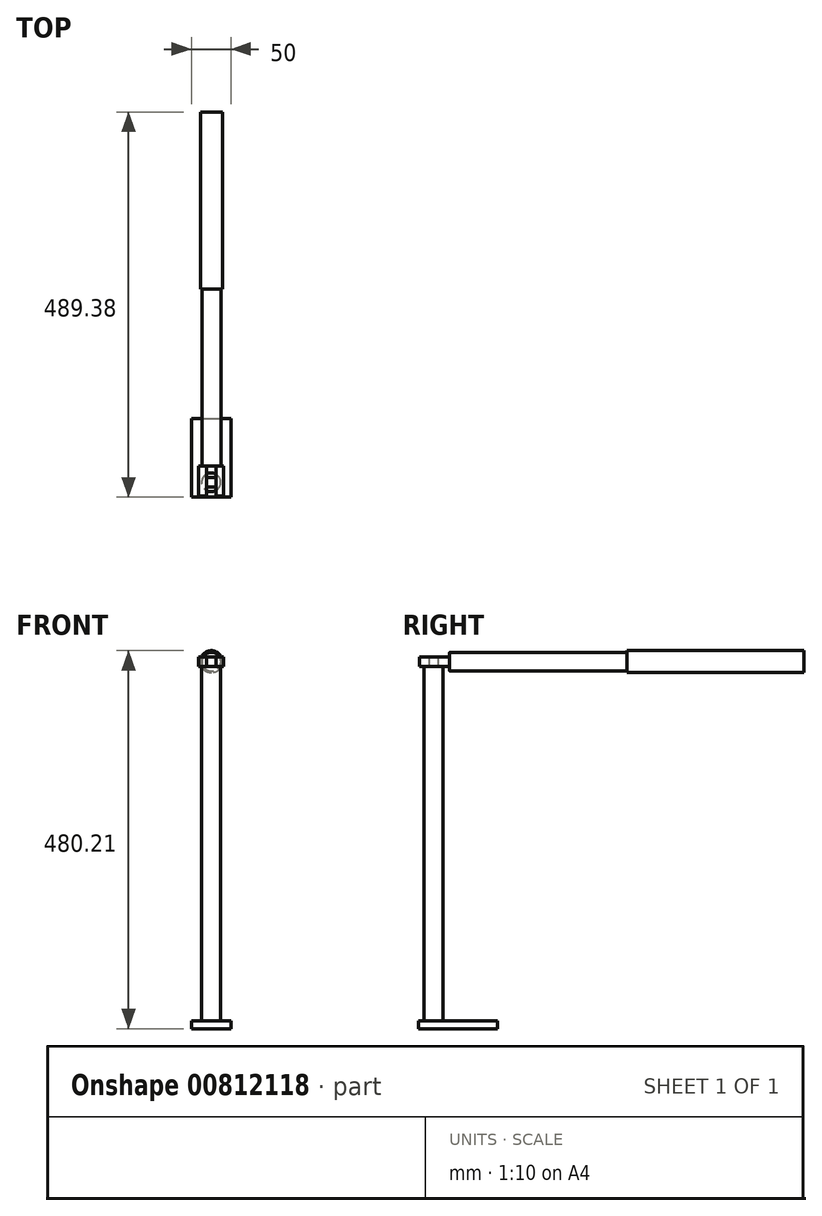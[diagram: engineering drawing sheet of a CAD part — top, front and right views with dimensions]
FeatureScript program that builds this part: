
annotation { "Feature Type Name" : "Feature", "Feature Type Description" : "" }
export const myFeature = defineFeature(function(context is Context, id is Id, definition is map)
    precondition{}
    {
        {
            var Q0;
            Q0=qCreatedBy(makeId("Top.planeOp"),FACE);
            var sketch = newSketch(context, id + "F0", { "sketchPlane" : qUnion([Q0])});
            skLineSegment(sketch, "E0.bottom", {"start": v(-96.82, -89.7) * mm, "end": v(-46.82, -89.7) * mm});
            skLineSegment(sketch, "E0.top", {"start": v(-96.82, 10.3) * mm, "end": v(-46.82, 10.3) * mm});
            skLineSegment(sketch, "E0.left", {"start": v(-96.82, -89.7) * mm, "end": v(-96.82, 10.3) * mm});
            skLineSegment(sketch, "E0.right", {"start": v(-46.82, -89.7) * mm, "end": v(-46.82, 10.3) * mm});
            skLineSegment(sketch, "E1.bottom", {"start": v(-96.82, 10.3) * mm, "end": v(-86.82, 10.3) * mm});
            skLineSegment(sketch, "E1.top", {"start": v(-96.82, 30.3) * mm, "end": v(-86.82, 30.3) * mm});
            skLineSegment(sketch, "E1.left", {"start": v(-96.82, 10.3) * mm, "end": v(-96.82, 30.3) * mm});
            skLineSegment(sketch, "E1.right", {"start": v(-86.82, 10.3) * mm, "end": v(-86.82, 30.3) * mm});
            skLineSegment(sketch, "E2.bottom", {"start": v(-46.82, 10.3) * mm, "end": v(-56.82, 10.3) * mm});
            skLineSegment(sketch, "E2.top", {"start": v(-46.82, 30.3) * mm, "end": v(-56.82, 30.3) * mm});
            skLineSegment(sketch, "E2.left", {"start": v(-46.82, 10.3) * mm, "end": v(-46.82, 30.3) * mm});
            skLineSegment(sketch, "E2.right", {"start": v(-56.82, 10.3) * mm, "end": v(-56.82, 30.3) * mm});
            skLineSegment(sketch, "E3.bottom", {"start": v(-86.82, 10.3) * mm, "end": v(-56.82, 10.3) * mm});
            skLineSegment(sketch, "E3.top", {"start": v(-86.82, 50.3) * mm, "end": v(-56.82, 50.3) * mm});
            skLineSegment(sketch, "E3.left", {"start": v(-86.82, 10.3) * mm, "end": v(-86.82, 50.3) * mm});
            skLineSegment(sketch, "E3.right", {"start": v(-56.82, 10.3) * mm, "end": v(-56.82, 50.3) * mm});
            skSolve(sketch);
        }
        {
            var Q0;
            Q0=makeQuery(id+"F0.imprint","IMPRINT",FACE,{"disambiguationData":[TD([[makeQuery(id+"F0.imprint","IMPRINT",EDGE,{"derivedFrom":sQuery(id+"F0.wireOp",EDGE,"E0.bottom")}),1.0]])]});
            var Q1;
            {var subQ0=sQuery(id+"F0.wireOp",EDGE,"E1.bottom");Q1=makeQuery(id+"F0.imprint","IMPRINT",FACE,{"disambiguationData":[TD([[makeQuery(id+"F0.imprint","IMPRINT",EDGE,{"derivedFrom":subQ0}),1.0]])]});}
            var Q2;
            {var subQ3=sQuery(id+"F0.wireOp",EDGE,"E3.bottom");Q2=makeQuery(id+"F0.imprint","IMPRINT",FACE,{"disambiguationData":[TD([[makeQuery(id+"F0.imprint","IMPRINT",EDGE,{"derivedFrom":subQ3}),1.0]])]});}
            var Q3;
            {var subQ0=sQuery(id+"F0.wireOp",EDGE,"E2.bottom");Q3=makeQuery(id+"F0.imprint","IMPRINT",FACE,{"disambiguationData":[TD([[makeQuery(id+"F0.imprint","IMPRINT",EDGE,{"derivedFrom":subQ0}),-1.0]])]});}
            extrude(context, id + "F1", {"entities" : qUnion([Q0, Q1, Q2, Q3]), "depth" : 10 * mm, "offsetDistance" : 25 * mm});
        }
        {
            var Q0;
            Q0=makeQuery(id+"F1.opExtrude","CAP_FACE",FACE,{"disambiguationData":[OSD([sQuery(id+"F0.wireOp",EDGE,"E0.bottom"),sQuery(id+"F0.wireOp",EDGE,"E0.left"),sQuery(id+"F0.wireOp",EDGE,"E0.right"),sQuery(id+"F0.wireOp",EDGE,"E1.top"),sQuery(id+"F0.wireOp",EDGE,"E1.left"),sQuery(id+"F0.wireOp",EDGE,"E2.top"),sQuery(id+"F0.wireOp",EDGE,"E2.left"),sQuery(id+"F0.wireOp",EDGE,"E3.top"),sQuery(id+"F0.wireOp",EDGE,"E3.left"),sQuery(id+"F0.wireOp",EDGE,"E3.right")])],"isStart":false});
            var sketch = newSketch(context, id + "F2", { "sketchPlane" : qUnion([Q0])});
            skCircle(sketch, "E4", {"center": v(-71.82, -70.8) * mm, "radius": 12 * mm});
            skPoint(sketch, "E4.centerSnap0", {"position": v(-71.82, -89.7) * mm});
            skSolve(sketch);
        }
        {
            var Q0;
            Q0=makeQuery(id+"F2.imprint","IMPRINT",FACE,{"disambiguationData":[TD([[makeQuery(id+"F2.imprint","IMPRINT",EDGE,{"derivedFrom":sQuery(id+"F2.wireOp",EDGE,"E4")}),1.0]])]});
            extrude(context, id + "F3", {"entities" : qUnion([Q0]), "operationType" : NewBodyOperationType.ADD, "depth" : 450 * mm, "offsetDistance" : 25 * mm});
        }
        {
            var Q0;
            Q0=makeQuery(id+"F3.opExtrude","CAP_FACE",FACE,{"disambiguationData":[OSD([sQuery(id+"F2.wireOp",EDGE,"E4")])],"isStart":false});
            var sketch = newSketch(context, id + "F4", { "sketchPlane" : qUnion([Q0])});
            skLineSegment(sketch, "E5.bottom", {"start": v(-77.82, -64.92) * mm, "end": v(-65.82, -64.92) * mm});
            skLineSegment(sketch, "E5.top", {"start": v(-77.82, -76.92) * mm, "end": v(-65.82, -76.92) * mm});
            skLineSegment(sketch, "E5.left", {"start": v(-77.82, -64.92) * mm, "end": v(-77.82, -76.92) * mm});
            skLineSegment(sketch, "E5.right", {"start": v(-65.82, -64.92) * mm, "end": v(-65.82, -76.92) * mm});
            skSolve(sketch);
        }
        {
            var Q0;
            Q0 = qSketchRegion(id + "F4", true);
            extrude(context, id + "F5", {"entities" : qUnion([Q0]), "operationType" : NewBodyOperationType.ADD, "depth" : 12 * mm, "offsetDistance" : 25 * mm});
        }
        {
            var Q0;
            Q0=makeQuery(id+"F5.opExtrude","SWEPT_FACE",FACE,{"disambiguationData":[OSD([sQuery(id+"F4.wireOp",EDGE,"E5.right")])]});
            var sketch = newSketch(context, id + "F6", { "sketchPlane" : qUnion([Q0])});
            skLineSegment(sketch, "E6.bottom", {"start": v(-88.4, 460) * mm, "end": v(-50.32, 460) * mm});
            skLineSegment(sketch, "E6.top", {"start": v(-88.4, 472.08) * mm, "end": v(-50.32, 472.08) * mm});
            skLineSegment(sketch, "E6.left", {"start": v(-88.4, 460) * mm, "end": v(-88.4, 472.08) * mm});
            skLineSegment(sketch, "E6.right", {"start": v(-50.32, 460) * mm, "end": v(-50.32, 472.08) * mm});
            skSolve(sketch);
        }
        {
            var Q0;
            Q0 = qSketchRegion(id + "F6", true);
            extrude(context, id + "F7", {"entities" : qUnion([Q0]), "operationType" : NewBodyOperationType.ADD, "depth" : 10 * mm, "offsetDistance" : 25 * mm});
        }
        {
            var Q0;
            Q0=makeQuery(id+"F5.opExtrude","SWEPT_FACE",FACE,{"disambiguationData":[OSD([sQuery(id+"F4.wireOp",EDGE,"E5.left")])]});
            var sketch = newSketch(context, id + "F8", { "sketchPlane" : qUnion([Q0])});
            skLineSegment(sketch, "E7.bottom", {"start": v(88.33, 460.09) * mm, "end": v(50.28, 460.09) * mm});
            skLineSegment(sketch, "E7.top", {"start": v(88.33, 472.12) * mm, "end": v(50.28, 472.12) * mm});
            skLineSegment(sketch, "E7.left", {"start": v(88.33, 460.09) * mm, "end": v(88.33, 472.12) * mm});
            skLineSegment(sketch, "E7.right", {"start": v(50.28, 460.09) * mm, "end": v(50.28, 472.12) * mm});
            skSolve(sketch);
        }
        {
            var Q0;
            Q0 = qSketchRegion(id + "F8", true);
            extrude(context, id + "F9", {"entities" : qUnion([Q0]), "operationType" : NewBodyOperationType.ADD, "depth" : 10 * mm, "offsetDistance" : 25 * mm});
        }
        {
            var Q0;
            Q0=makeQuery(id+"F7.opExtrude","SWEPT_FACE",FACE,{"disambiguationData":[OSD([sQuery(id+"F6.wireOp",EDGE,"E6.right")])]});
            var sketch = newSketch(context, id + "F10", { "sketchPlane" : qUnion([Q0])});
            skCircle(sketch, "E8", {"center": v(71.53, 466.21) * mm, "radius": 12 * mm});
            skSolve(sketch);
        }
        {
            var Q0;
            Q0 = qSketchRegion(id + "F10", true);
            extrude(context, id + "F11", {"entities" : qUnion([Q0]), "operationType" : NewBodyOperationType.ADD, "depth" : 225 * mm, "offsetDistance" : 25 * mm});
        }
        {
            var Q0;
            Q0=makeQuery(id+"F11.opExtrude","CAP_FACE",FACE,{"disambiguationData":[OSD([sQuery(id+"F10.wireOp",EDGE,"E8")])],"isStart":false});
            var sketch = newSketch(context, id + "F12", { "sketchPlane" : qUnion([Q0])});
            skCircle(sketch, "E9", {"center": v(71.53, 466.21) * mm, "radius": 14 * mm});
            skSolve(sketch);
        }
        {
            var Q0;
            Q0 = qSketchRegion(id + "F12", true);
            extrude(context, id + "F13", {"entities" : qUnion([Q0]), "operationType" : NewBodyOperationType.ADD, "depth" : 225 * mm, "offsetDistance" : 25 * mm});
        }
    });
